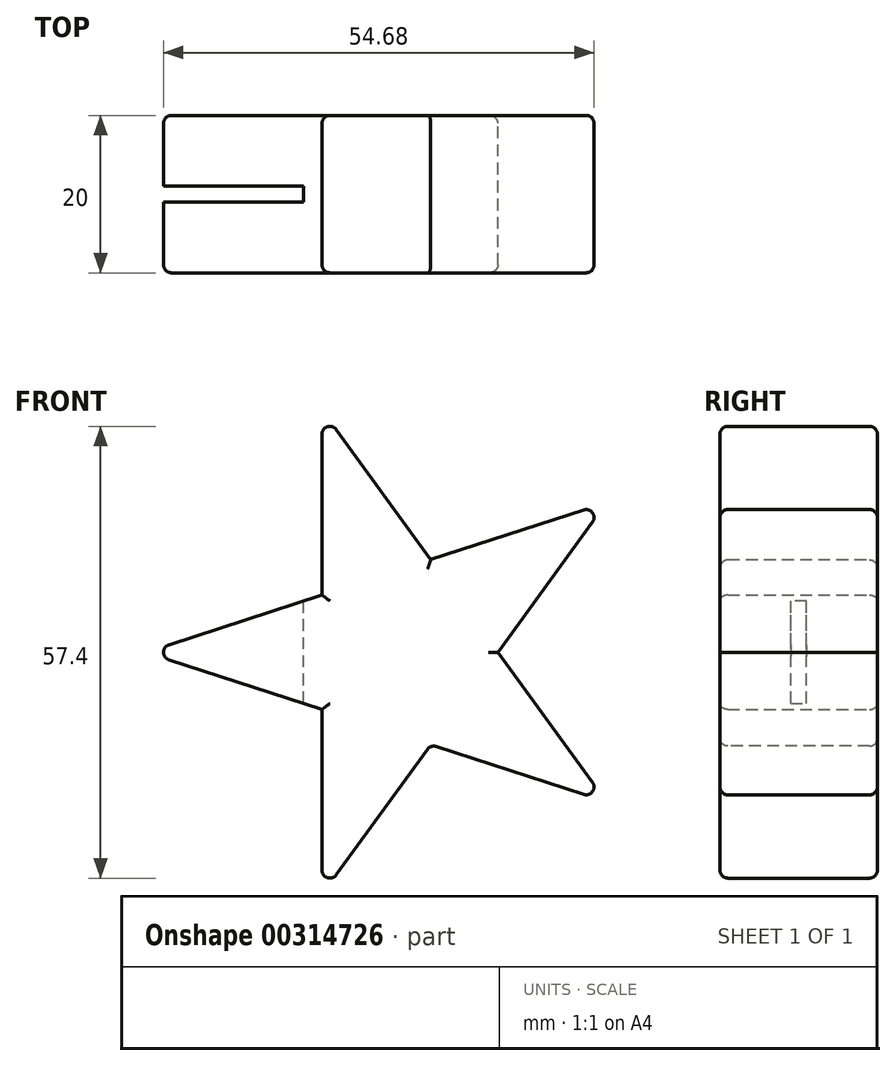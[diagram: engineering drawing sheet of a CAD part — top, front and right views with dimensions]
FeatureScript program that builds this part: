
annotation { "Feature Type Name" : "Feature", "Feature Type Description" : "" }
export const myFeature = defineFeature(function(context is Context, id is Id, definition is map)
    precondition{}
    {
        {
            var Q0;
            Q0=qCreatedBy(makeId("Front.planeOp"),FACE);
            var sketch = newSketch(context, id + "F0", { "sketchPlane" : qUnion([Q0])});
            skCircle(sketch, "E0.cCircle", {"center": v(0, 0) * mm, "radius": 10 * mm, "construction": true});
            skLineSegment(sketch, "E0.0", {"start": v(-10, -30.78) * mm, "end": v(-10, -7.27) * mm});
            skLineSegment(sketch, "E0.1", {"start": v(-32.36, 0) * mm, "end": v(-10, 7.27) * mm});
            skLineSegment(sketch, "E0.2", {"start": v(-10, 30.78) * mm, "end": v(3.82, 11.76) * mm});
            skLineSegment(sketch, "E0.3", {"start": v(26.18, 19.02) * mm, "end": v(12.36, 0) * mm});
            skLineSegment(sketch, "E0.4", {"start": v(26.18, -19.02) * mm, "end": v(3.82, -11.76) * mm});
            skPoint(sketch, "E0.0.midPoint", {"position": v(-10, 0) * mm});
            skPoint(sketch, "E1.orphan", {"position": v(12.36, 0) * mm});
            skPoint(sketch, "E2.orphan", {"position": v(3.82, -11.76) * mm});
            skPoint(sketch, "E3.orphan", {"position": v(-10, -7.27) * mm});
            skPoint(sketch, "E4.orphan", {"position": v(3.82, 11.76) * mm});
            skPoint(sketch, "E5.orphan", {"position": v(-10, 7.27) * mm});
            skLineSegment(sketch, "E6.trimOffspring", {"start": v(3.82, 11.76) * mm, "end": v(26.18, 19.02) * mm});
            skLineSegment(sketch, "E7.trimOffspring", {"start": v(12.36, 0) * mm, "end": v(26.18, -19.02) * mm});
            skLineSegment(sketch, "E8.trimOffspring", {"start": v(3.82, -11.76) * mm, "end": v(-10, -30.78) * mm});
            skLineSegment(sketch, "E9.trimOffspring", {"start": v(-10, -7.27) * mm, "end": v(-32.36, 0) * mm});
            skLineSegment(sketch, "E10.trimOffspring", {"start": v(-10, 7.27) * mm, "end": v(-10, 30.78) * mm});
            skSolve(sketch);
        }
        {
            var Q0;
            Q0 = qSketchRegion(id + "F0", true);
            extrude(context, id + "F1", {"entities" : qUnion([Q0]), "depth" : 20 * mm});
        }
        {
            var Q0;
            Q0=qCreatedBy(makeId("Top.planeOp"),FACE);
            var sketch = newSketch(context, id + "F2", { "sketchPlane" : qUnion([Q0])});
            skLineSegment(sketch, "E11.bottom", {"start": v(-32.36, -9) * mm, "end": v(-12.36, -9) * mm});
            skLineSegment(sketch, "E11.top", {"start": v(-32.36, -11) * mm, "end": v(-12.36, -11) * mm});
            skLineSegment(sketch, "E11.left", {"start": v(-32.36, -9) * mm, "end": v(-32.36, -11) * mm});
            skLineSegment(sketch, "E11.right", {"start": v(-12.36, -9) * mm, "end": v(-12.36, -11) * mm});
            skSolve(sketch);
        }
        {
            var Q0;
            Q0 = qSketchRegion(id + "F2", true);
            extrude(context, id + "F3", {"entities" : qUnion([Q0]), "operationType" : NewBodyOperationType.REMOVE, "endBound" : BoundingType.SYMMETRIC, "oppositeDirection" : true, "depth" : 25 * mm});
        }
        {
            var Q0;
            Q0=makeQuery(id+"F1.opExtrude","CAP_EDGE",EDGE,{"disambiguationData":[OSD([sQuery(id+"F0.wireOp",EDGE,"E9.trimOffspring")])],"isStart":true});
            var Q1;
            Q1=makeQuery(id+"F1.opExtrude","CAP_EDGE",EDGE,{"disambiguationData":[OSD([sQuery(id+"F0.wireOp",EDGE,"E0.1")])],"isStart":true});
            var Q2;
            Q2=makeQuery(id+"F1.opExtrude","CAP_EDGE",EDGE,{"disambiguationData":[OSD([sQuery(id+"F0.wireOp",EDGE,"E10.trimOffspring")])],"isStart":true});
            var Q3;
            Q3=makeQuery(id+"F1.opExtrude","CAP_EDGE",EDGE,{"disambiguationData":[OSD([sQuery(id+"F0.wireOp",EDGE,"E0.2")])],"isStart":true});
            var Q4;
            Q4=makeQuery(id+"F1.opExtrude","CAP_EDGE",EDGE,{"disambiguationData":[OSD([sQuery(id+"F0.wireOp",EDGE,"E6.trimOffspring")])],"isStart":true});
            var Q5;
            Q5=makeQuery(id+"F1.opExtrude","CAP_EDGE",EDGE,{"disambiguationData":[OSD([sQuery(id+"F0.wireOp",EDGE,"E0.3")])],"isStart":true});
            var Q6;
            Q6=makeQuery(id+"F1.opExtrude","CAP_EDGE",EDGE,{"disambiguationData":[OSD([sQuery(id+"F0.wireOp",EDGE,"E7.trimOffspring")])],"isStart":true});
            var Q7;
            Q7=makeQuery(id+"F1.opExtrude","CAP_EDGE",EDGE,{"disambiguationData":[OSD([sQuery(id+"F0.wireOp",EDGE,"E0.4")])],"isStart":true});
            var Q8;
            Q8=makeQuery(id+"F1.opExtrude","CAP_EDGE",EDGE,{"disambiguationData":[OSD([sQuery(id+"F0.wireOp",EDGE,"E8.trimOffspring")])],"isStart":true});
            var Q9;
            Q9=makeQuery(id+"F1.opExtrude","CAP_EDGE",EDGE,{"disambiguationData":[OSD([sQuery(id+"F0.wireOp",EDGE,"E0.0")])],"isStart":true});
            var Q10;
            Q10=makeQuery(id+"F1.opExtrude","CAP_EDGE",EDGE,{"disambiguationData":[OSD([sQuery(id+"F0.wireOp",EDGE,"E0.1")])],"isStart":false});
            var Q11;
            Q11=makeQuery(id+"F1.opExtrude","CAP_EDGE",EDGE,{"disambiguationData":[OSD([sQuery(id+"F0.wireOp",EDGE,"E9.trimOffspring")])],"isStart":false});
            var Q12;
            Q12=makeQuery(id+"F1.opExtrude","CAP_EDGE",EDGE,{"disambiguationData":[OSD([sQuery(id+"F0.wireOp",EDGE,"E0.0")])],"isStart":false});
            var Q13;
            Q13=makeQuery(id+"F1.opExtrude","CAP_EDGE",EDGE,{"disambiguationData":[OSD([sQuery(id+"F0.wireOp",EDGE,"E8.trimOffspring")])],"isStart":false});
            var Q14;
            Q14=makeQuery(id+"F1.opExtrude","CAP_EDGE",EDGE,{"disambiguationData":[OSD([sQuery(id+"F0.wireOp",EDGE,"E0.4")])],"isStart":false});
            var Q15;
            Q15=makeQuery(id+"F1.opExtrude","CAP_EDGE",EDGE,{"disambiguationData":[OSD([sQuery(id+"F0.wireOp",EDGE,"E7.trimOffspring")])],"isStart":false});
            var Q16;
            Q16=makeQuery(id+"F1.opExtrude","CAP_EDGE",EDGE,{"disambiguationData":[OSD([sQuery(id+"F0.wireOp",EDGE,"E0.3")])],"isStart":false});
            var Q17;
            Q17=makeQuery(id+"F1.opExtrude","CAP_EDGE",EDGE,{"disambiguationData":[OSD([sQuery(id+"F0.wireOp",EDGE,"E6.trimOffspring")])],"isStart":false});
            var Q18;
            Q18=makeQuery(id+"F1.opExtrude","CAP_EDGE",EDGE,{"disambiguationData":[OSD([sQuery(id+"F0.wireOp",EDGE,"E0.2")])],"isStart":false});
            var Q19;
            Q19=makeQuery(id+"F1.opExtrude","CAP_EDGE",EDGE,{"disambiguationData":[OSD([sQuery(id+"F0.wireOp",EDGE,"E10.trimOffspring")])],"isStart":false});
            var Q20;
            Q20=makeQuery(id+"F1.opExtrude","SWEPT_EDGE",EDGE,{"disambiguationData":[OSD([sQuery(id+"F0.wireOp",EDGE,"E0.0"),sQuery(id+"F0.wireOp",EDGE,"E8.trimOffspring")])]});
            var Q21;
            Q21=makeQuery(id+"F1.opExtrude","SWEPT_EDGE",EDGE,{"disambiguationData":[OSD([sQuery(id+"F0.wireOp",EDGE,"E0.4"),sQuery(id+"F0.wireOp",EDGE,"E8.trimOffspring")])]});
            var Q22;
            {var subQ0=sQuery(id+"F0.wireOp",EDGE,"E9.trimOffspring");var subQ1=sQuery(id+"F0.wireOp",EDGE,"E0.1");Q22=makeQuery(id+"F3.boolean.opBoolean","SPLIT",EDGE,{"disambiguationData":[TD([makeQuery(id+"F3.opExtrude","SWEPT_FACE",FACE,{"disambiguationData":[OSD([sQuery(id+"F2.wireOp",EDGE,"E11.bottom")])]})])],"derivedFrom":makeQuery(id+"F1.opExtrude","SWEPT_EDGE",EDGE,{"disambiguationData":[OSD([subQ1,subQ0])]})});}
            var Q23;
            {var subQ0=sQuery(id+"F0.wireOp",EDGE,"E9.trimOffspring");var subQ1=sQuery(id+"F0.wireOp",EDGE,"E0.1");Q23=makeQuery(id+"F3.boolean.opBoolean","SPLIT",EDGE,{"disambiguationData":[TD([makeQuery(id+"F3.opExtrude","SWEPT_FACE",FACE,{"disambiguationData":[OSD([sQuery(id+"F2.wireOp",EDGE,"E11.top")])]})])],"derivedFrom":makeQuery(id+"F1.opExtrude","SWEPT_EDGE",EDGE,{"disambiguationData":[OSD([subQ1,subQ0])]})});}
            var Q24;
            Q24=makeQuery(id+"F1.opExtrude","SWEPT_EDGE",EDGE,{"disambiguationData":[OSD([sQuery(id+"F0.wireOp",EDGE,"E0.2"),sQuery(id+"F0.wireOp",EDGE,"E10.trimOffspring")])]});
            var Q25;
            Q25=makeQuery(id+"F1.opExtrude","SWEPT_EDGE",EDGE,{"disambiguationData":[OSD([sQuery(id+"F0.wireOp",EDGE,"E0.3"),sQuery(id+"F0.wireOp",EDGE,"E6.trimOffspring")])]});
            var Q26;
            Q26=makeQuery(id+"F1.opExtrude","SWEPT_EDGE",EDGE,{"disambiguationData":[OSD([sQuery(id+"F0.wireOp",EDGE,"E0.4"),sQuery(id+"F0.wireOp",EDGE,"E7.trimOffspring")])]});
            fillet(context, id + "F4", {"entities" : qUnion([Q0, Q1, Q2, Q3, Q4, Q5, Q6, Q7, Q8, Q9, Q10, Q11, Q12, Q13, Q14, Q15, Q16, Q17, Q18, Q19, Q20, Q21, Q22, Q23, Q24, Q25, Q26]), "radius" : 1 * mm, "tangentPropagation" : true, "allowEdgeOverflow" : false});
        }
    });
